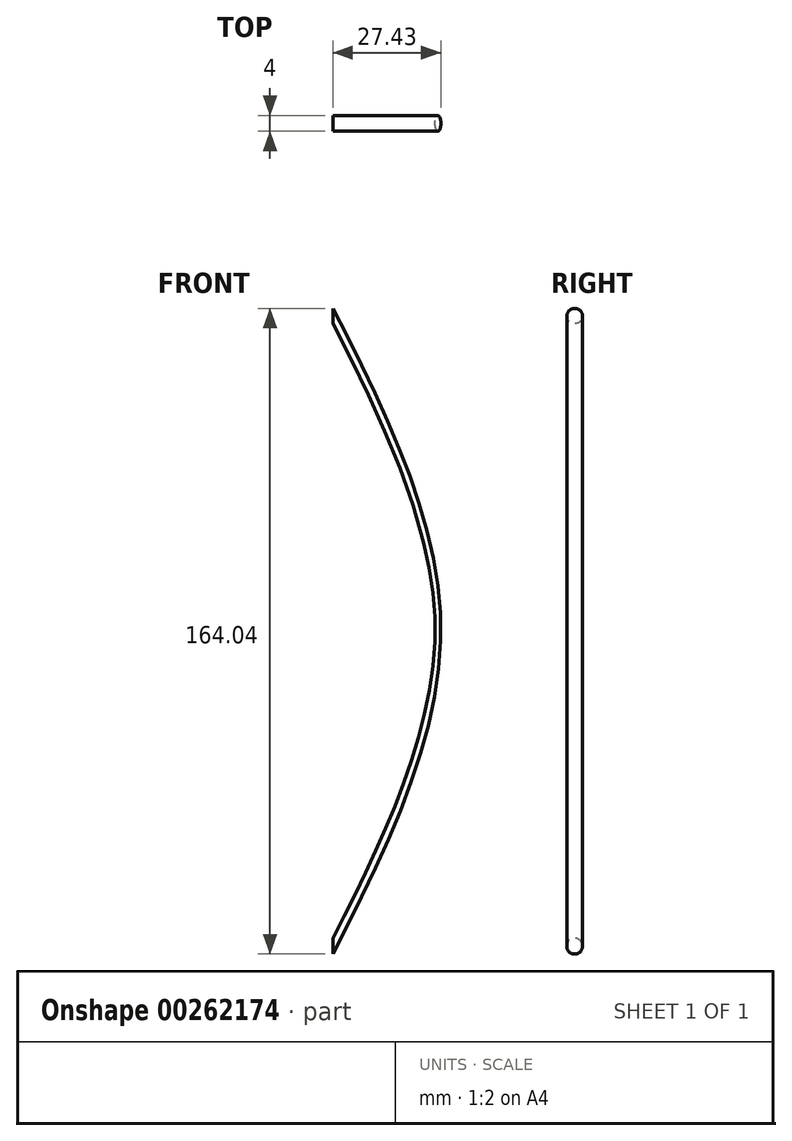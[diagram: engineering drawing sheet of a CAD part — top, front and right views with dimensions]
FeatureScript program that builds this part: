
annotation { "Feature Type Name" : "Feature", "Feature Type Description" : "" }
export const myFeature = defineFeature(function(context is Context, id is Id, definition is map)
    precondition{}
    {
        {
            var Q0;
            Q0=qCreatedBy(makeId("Front.planeOp"),FACE);
            var sketch = newSketch(context, id + "F0", { "sketchPlane" : qUnion([Q0])});
            skLineSegment(sketch, "E0", {"start": v(0, 0) * mm, "end": v(31, 0) * mm});
            skFitSpline(sketch, "E1", {"points": [v(0, 90.5) * mm, v(31, 0) * mm, v(0, -90.5) * mm], "startDerivative": vector(93, -181) * mm, "endDerivative": vector(-93, -181) * mm});
            skSolve(sketch);
        }
        {
            var Q0;
            Q0=qCreatedBy(makeId("Right.planeOp"),FACE);
            var sketch = newSketch(context, id + "F1", { "sketchPlane" : qUnion([Q0])});
            skLineSegment(sketch, "E2.bottom", {"start": v(5, -90.5) * mm, "end": v(-5, -90.5) * mm});
            skLineSegment(sketch, "E2.top", {"start": v(5, 90.5) * mm, "end": v(-5, 90.5) * mm, "construction": true});
            skLineSegment(sketch, "E2.left", {"start": v(5, -90.5) * mm, "end": v(5, 90.5) * mm});
            skLineSegment(sketch, "E2.right", {"start": v(-5, -90.5) * mm, "end": v(-5, 90.5) * mm});
            skPoint(sketch, "E2.middle", {"position": v(0, 0) * mm});
            skLineSegment(sketch, "E3", {"start": v(0, 90.5) * mm, "end": v(0, -90.5) * mm, "construction": true});
            skCircle(sketch, "E4", {"center": v(0, 80) * mm, "radius": 2 * mm});
            skCircle(sketch, "E5.MirrorC", {"center": v(0, -80) * mm, "radius": 2 * mm});
            skLineSegment(sketch, "E6.top", {"start": v(5, -70.5) * mm, "end": v(-5, -70.5) * mm});
            skLineSegment(sketch, "E6.left", {"start": v(5, -90.5) * mm, "end": v(5, -70.5) * mm});
            skLineSegment(sketch, "E6.right", {"start": v(-5, -90.5) * mm, "end": v(-5, -70.5) * mm});
            skSolve(sketch);
        }
        {
            var Q0;
            Q0=makeQuery(id+"F1.imprint","IMPRINT",FACE,{"disambiguationData":[TD([[makeQuery(id+"F1.imprint","IMPRINT",EDGE,{"derivedFrom":sQuery(id+"F1.wireOp",EDGE,"E5.MirrorC")}),1.0]])]});
            var Q1;
            Q1=sQuery(id+"F0.wireOp",EDGE,"E1");
            sweep(context, id + "F2", {"profiles" : qUnion([Q0]), "path" : qUnion([Q1])});
        }
        {
            var Q0;
            Q0=qCreatedBy(makeId("Right.planeOp"),FACE);
            var sketch = newSketch(context, id + "F3", { "sketchPlane" : qUnion([Q0])});
            skLineSegment(sketch, "E7.bottom", {"start": v(-152.9, 111.43) * mm, "end": v(35.87, 111.43) * mm});
            skLineSegment(sketch, "E7.top", {"start": v(-152.9, 44.05) * mm, "end": v(35.87, 44.05) * mm});
            skLineSegment(sketch, "E7.left", {"start": v(-152.9, 111.43) * mm, "end": v(-152.9, 44.05) * mm});
            skLineSegment(sketch, "E7.right", {"start": v(35.87, 111.43) * mm, "end": v(35.87, 44.05) * mm});
            skSolve(sketch);
        }
        {
            var Q0;
            Q0=makeQuery(id+"F3.imprint","IMPRINT",FACE,{"disambiguationData":[TD([[makeQuery(id+"F3.imprint","IMPRINT",EDGE,{"derivedFrom":sQuery(id+"F3.wireOp",EDGE,"E7.bottom")}),-1.0]])]});
            extrude(context, id + "F4", {"entities" : qUnion([Q0]), "operationType" : NewBodyOperationType.REMOVE, "oppositeDirection" : true, "depth" : 25 * mm});
        }
    });
